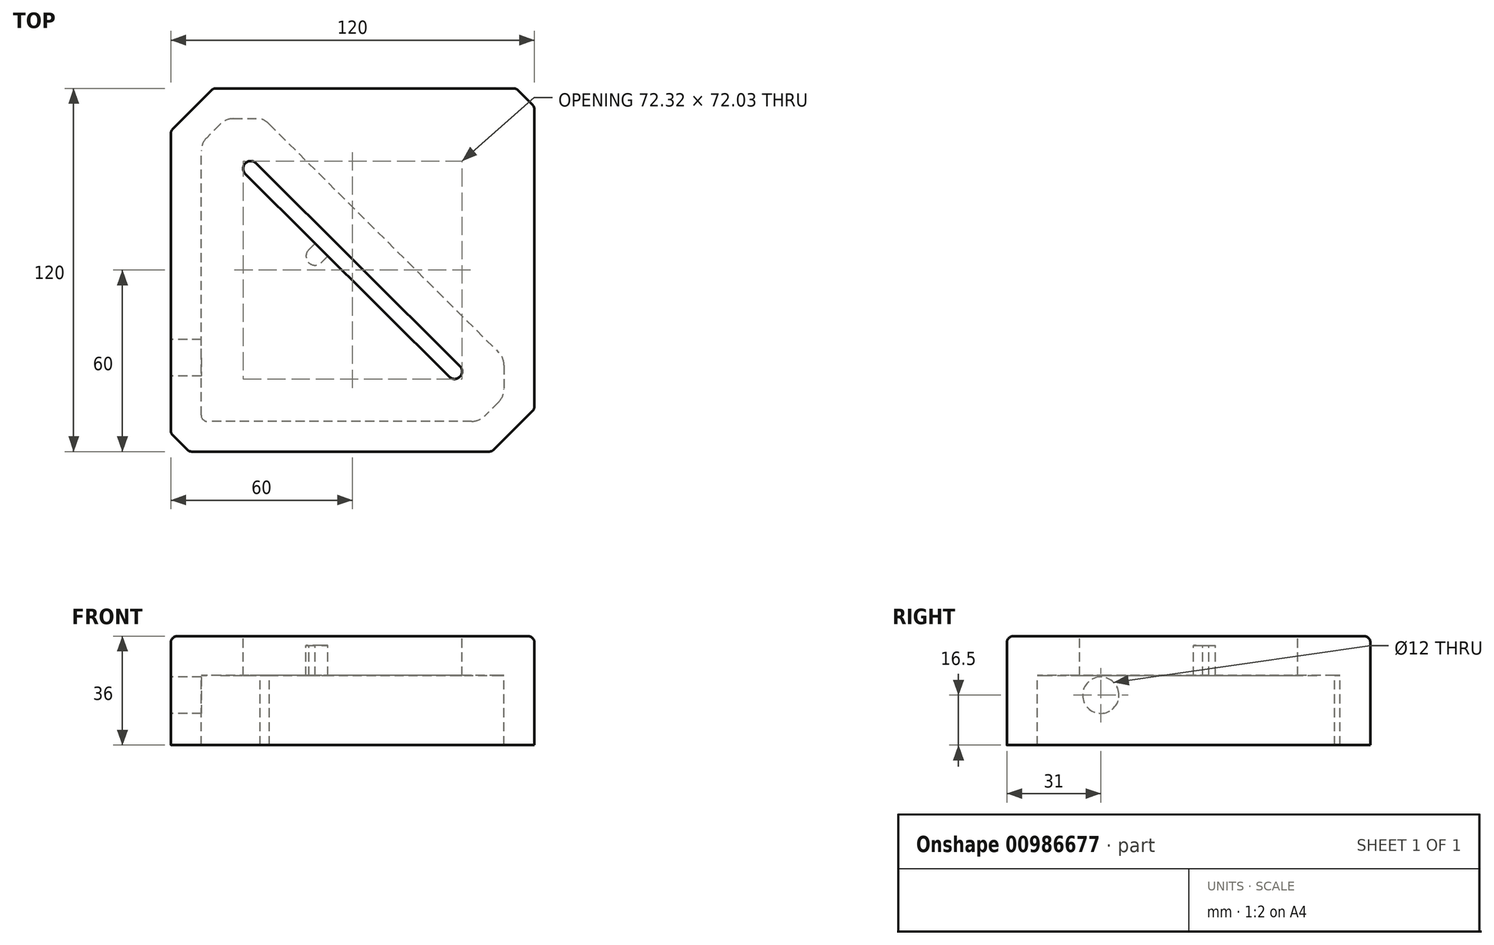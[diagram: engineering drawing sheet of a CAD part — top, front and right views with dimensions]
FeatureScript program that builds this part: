
annotation { "Feature Type Name" : "Feature", "Feature Type Description" : "" }
export const myFeature = defineFeature(function(context is Context, id is Id, definition is map)
    precondition{}
    {
        {
            var Q0;
            Q0=qCreatedBy(makeId("Top.planeOp"),FACE);
            var sketch = newSketch(context, id + "F0", { "sketchPlane" : qUnion([Q0])});
            skLineSegment(sketch, "E0.bottom", {"start": v(14, 0) * mm, "end": v(114, 0) * mm});
            skLineSegment(sketch, "E0.top", {"start": v(6, 120) * mm, "end": v(106, 120) * mm});
            skLineSegment(sketch, "E0.left", {"start": v(0, 14) * mm, "end": v(0, 114) * mm});
            skLineSegment(sketch, "E0.right", {"start": v(120, 6) * mm, "end": v(120, 106) * mm});
            skLineSegment(sketch, "E1", {"start": v(0, 114) * mm, "end": v(6, 120) * mm});
            skLineSegment(sketch, "E2", {"start": v(120, 6) * mm, "end": v(114, 0) * mm});
            skLineSegment(sketch, "E3", {"start": v(0, 14) * mm, "end": v(14, 0) * mm});
            skLineSegment(sketch, "E4", {"start": v(106, 120) * mm, "end": v(120, 106) * mm});
            skLineSegment(sketch, "E5.left", {"start": v(95.43, 91.74) * mm, "end": v(28.1, 24.72) * mm});
            skLineSegment(sketch, "E5.right", {"start": v(91.9, 95.28) * mm, "end": v(24.57, 28.26) * mm});
            skPoint(sketch, "E5.middle", {"position": v(60, 60) * mm});
            skArc(sketch, "E6", {"start": v(95.43, 91.74) * mm, "mid": v(95.43, 95.28) * mm, "end": v(91.9, 95.28) * mm});
            skArc(sketch, "E7", {"start": v(24.57, 28.26) * mm, "mid": v(24.57, 24.72) * mm, "end": v(28.1, 24.72) * mm});
            skLineSegment(sketch, "E8", {"start": v(32.45, 11.8) * mm, "end": v(108.23, 87.24) * mm});
            skLineSegment(sketch, "E9", {"start": v(110, 91.5) * mm, "end": v(110, 99.37) * mm});
            skLineSegment(sketch, "E10", {"start": v(99.37, 110) * mm, "end": v(12, 110) * mm});
            skLineSegment(sketch, "E11", {"start": v(10, 108) * mm, "end": v(10, 20.63) * mm});
            skLineSegment(sketch, "E12", {"start": v(20.63, 10) * mm, "end": v(29.51, 10) * mm});
            skArc(sketch, "E13", {"start": v(29.51, 10) * mm, "mid": v(31.1, 10.7) * mm, "end": v(32.45, 11.8) * mm});
            skPoint(sketch, "E14.orphan", {"position": v(10, 10) * mm});
            skPoint(sketch, "E15.orphan", {"position": v(30.65, 10) * mm});
            skArc(sketch, "E16", {"start": v(12, 110) * mm, "mid": v(10.59, 109.41) * mm, "end": v(10, 108) * mm});
            skArc(sketch, "E17", {"start": v(49.63, 53.2) * mm, "mid": v(49.73, 53.3) * mm, "end": v(49.84, 53.4) * mm});
            skArc(sketch, "E18.trimOffspring", {"start": v(49.8, 57.48) * mm, "mid": v(45.5, 57.56) * mm, "end": v(45.55, 53.26) * mm});
            skLineSegment(sketch, "E19", {"start": v(49.8, 57.48) * mm, "end": v(51.8, 55.36) * mm});
            skLineSegment(sketch, "E20", {"start": v(45.55, 53.26) * mm, "end": v(47.6, 51.19) * mm});
            skLineSegment(sketch, "E21", {"start": v(108.24, 103.62) * mm, "end": v(103.62, 108.24) * mm});
            skLineSegment(sketch, "E22", {"start": v(16.38, 11.76) * mm, "end": v(11.76, 16.38) * mm});
            skPoint(sketch, "E23.visualSharp", {"position": v(18.14, 10) * mm});
            skArc(sketch, "E23.filletArc", {"start": v(16.38, 11.76) * mm, "mid": v(18.33, 10.46) * mm, "end": v(20.63, 10) * mm});
            skPoint(sketch, "E24.visualSharp", {"position": v(10, 18.14) * mm});
            skArc(sketch, "E24.filletArc", {"start": v(10, 20.63) * mm, "mid": v(10.46, 18.33) * mm, "end": v(11.76, 16.38) * mm});
            skPoint(sketch, "E25.visualSharp", {"position": v(110, 101.86) * mm});
            skArc(sketch, "E25.filletArc", {"start": v(110, 99.37) * mm, "mid": v(109.54, 101.67) * mm, "end": v(108.24, 103.62) * mm});
            skPoint(sketch, "E26.visualSharp", {"position": v(101.86, 110) * mm});
            skArc(sketch, "E26.filletArc", {"start": v(103.62, 108.24) * mm, "mid": v(101.67, 109.54) * mm, "end": v(99.37, 110) * mm});
            skPoint(sketch, "E27.visualSharp", {"position": v(110, 89) * mm});
            skArc(sketch, "E27.filletArc", {"start": v(108.23, 87.24) * mm, "mid": v(109.54, 89.2) * mm, "end": v(110, 91.5) * mm});
            skSolve(sketch);
        }
        {
            var Q0;
            Q0=makeQuery(id+"F0.imprint","IMPRINT",FACE,{"disambiguationData":[TD([[makeQuery(id+"F0.imprint","IMPRINT",EDGE,{"derivedFrom":sQuery(id+"F0.wireOp",EDGE,"E5.left")}),1.0]])]});
            extrude(context, id + "F1", {"entities" : qUnion([Q0]), "depth" : 13 * mm, "offsetDistance" : 25 * mm});
        }
        {
            var Q0;
            Q0=makeQuery(id+"F0.imprint","IMPRINT",FACE,{"disambiguationData":[TD([[makeQuery(id+"F0.imprint","IMPRINT",EDGE,{"derivedFrom":sQuery(id+"F0.wireOp",EDGE,"E0.bottom")}),1.0]])]});
            extrude(context, id + "F2", {"entities" : qUnion([Q0]), "operationType" : NewBodyOperationType.ADD, "depth" : 36 * mm, "offsetDistance" : 25 * mm});
        }
        {
            var Q0;
            {var subQ4=sQuery(id+"F0.wireOp",EDGE,"E17");var subQ5=sQuery(id+"F0.wireOp",EDGE,"E5.right");var subQ8=makeQuery(id+"F0.imprint","INTERSECT",VERTEX,{"disambiguationData":[OD(1.0)],"derivedFrom":[subQ5,subQ4]});Q0=makeQuery(id+"F0.imprint","IMPRINT",FACE,{"disambiguationData":[TD([[makeQuery(id+"F0.imprint","IMPRINT",EDGE,{"disambiguationData":[TD([[subQ8,1.0]])],"derivedFrom":subQ5}),-1.0]])]});}
            extrude(context, id + "F3", {"entities" : qUnion([Q0]), "operationType" : NewBodyOperationType.ADD, "depth" : 3 * mm, "offsetDistance" : 25 * mm});
        }
        {
            var Q0;
            Q0=makeQuery(id+"F2.opExtrude","CAP_EDGE",EDGE,{"disambiguationData":[OSD([sQuery(id+"F0.wireOp",EDGE,"E0.top")])],"isStart":true});
            var Q1;
            Q1=makeQuery(id+"F2.opExtrude","SWEPT_EDGE",EDGE,{"disambiguationData":[OSD([sQuery(id+"F0.wireOp",EDGE,"E0.top"),sQuery(id+"F0.wireOp",EDGE,"E4")])]});
            var Q2;
            Q2=makeQuery(id+"F2.opExtrude","SWEPT_EDGE",EDGE,{"disambiguationData":[OSD([sQuery(id+"F0.wireOp",EDGE,"E0.right"),sQuery(id+"F0.wireOp",EDGE,"E4")])]});
            var Q3;
            Q3=makeQuery(id+"F2.opExtrude","CAP_EDGE",EDGE,{"disambiguationData":[OSD([sQuery(id+"F0.wireOp",EDGE,"E0.right")])],"isStart":true});
            var Q4;
            Q4=makeQuery(id+"F2.opExtrude","CAP_EDGE",EDGE,{"disambiguationData":[OSD([sQuery(id+"F0.wireOp",EDGE,"E4")])],"isStart":true});
            var Q5;
            Q5=makeQuery(id+"F2.opExtrude","CAP_EDGE",EDGE,{"disambiguationData":[OSD([sQuery(id+"F0.wireOp",EDGE,"E2")])],"isStart":true});
            var Q6;
            Q6=makeQuery(id+"F2.opExtrude","SWEPT_EDGE",EDGE,{"disambiguationData":[OSD([sQuery(id+"F0.wireOp",EDGE,"E0.bottom"),sQuery(id+"F0.wireOp",EDGE,"E2")])]});
            var Q7;
            Q7=makeQuery(id+"F2.opExtrude","SWEPT_EDGE",EDGE,{"disambiguationData":[OSD([sQuery(id+"F0.wireOp",EDGE,"E0.right"),sQuery(id+"F0.wireOp",EDGE,"E2")])]});
            var Q8;
            Q8=makeQuery(id+"F2.opExtrude","CAP_EDGE",EDGE,{"disambiguationData":[OSD([sQuery(id+"F0.wireOp",EDGE,"E0.bottom")])],"isStart":true});
            var Q9;
            Q9=makeQuery(id+"F2.opExtrude","SWEPT_EDGE",EDGE,{"disambiguationData":[OSD([sQuery(id+"F0.wireOp",EDGE,"E0.bottom"),sQuery(id+"F0.wireOp",EDGE,"E3")])]});
            var Q10;
            Q10=makeQuery(id+"F2.opExtrude","CAP_EDGE",EDGE,{"disambiguationData":[OSD([sQuery(id+"F0.wireOp",EDGE,"E3")])],"isStart":true});
            var Q11;
            Q11=makeQuery(id+"F2.opExtrude","SWEPT_EDGE",EDGE,{"disambiguationData":[OSD([sQuery(id+"F0.wireOp",EDGE,"E0.left"),sQuery(id+"F0.wireOp",EDGE,"E3")])]});
            var Q12;
            Q12=makeQuery(id+"F2.opExtrude","CAP_EDGE",EDGE,{"disambiguationData":[OSD([sQuery(id+"F0.wireOp",EDGE,"E0.left")])],"isStart":true});
            var Q13;
            Q13=makeQuery(id+"F2.opExtrude","CAP_EDGE",EDGE,{"disambiguationData":[OSD([sQuery(id+"F0.wireOp",EDGE,"E1")])],"isStart":true});
            var Q14;
            Q14=makeQuery(id+"F2.opExtrude","SWEPT_EDGE",EDGE,{"disambiguationData":[OSD([sQuery(id+"F0.wireOp",EDGE,"E0.left"),sQuery(id+"F0.wireOp",EDGE,"E1")])]});
            var Q15;
            Q15=makeQuery(id+"F2.opExtrude","SWEPT_EDGE",EDGE,{"disambiguationData":[OSD([sQuery(id+"F0.wireOp",EDGE,"E0.top"),sQuery(id+"F0.wireOp",EDGE,"E1")])]});
            fillet(context, id + "F4", {"entities" : qUnion([Q0, Q1, Q2, Q3, Q4, Q5, Q6, Q7, Q8, Q9, Q10, Q11, Q12, Q13, Q14, Q15]), "radius" : 2 * mm, "tangentPropagation" : true, "allowEdgeOverflow" : false});
        }
        {
            var Q0;
            Q0=makeQuery(id+"F2.opExtrude","SWEPT_FACE",FACE,{"disambiguationData":[OSD([sQuery(id+"F0.wireOp",EDGE,"E0.left")])]});
            var sketch = newSketch(context, id + "F5", { "sketchPlane" : qUnion([Q0])});
            skCircle(sketch, "E28", {"center": v(-89, 19.5) * mm, "radius": 6 * mm});
            skSolve(sketch);
        }
        {
            var Q0;
            Q0=sQuery(id+"F5.wireOp",VERTEX,"E28.center");
            var Q1;
            Q1=makeQuery(id+"F1.opExtrude","SWEPT_BODY",BODY,{"disambiguationData":[OSD([sQuery(id+"F0.wireOp",EDGE,"E5.left"),sQuery(id+"F0.wireOp",EDGE,"E5.right"),sQuery(id+"F0.wireOp",EDGE,"E6"),sQuery(id+"F0.wireOp",EDGE,"E7"),sQuery(id+"F0.wireOp",EDGE,"E8"),sQuery(id+"F0.wireOp",EDGE,"E9"),sQuery(id+"F0.wireOp",EDGE,"E10"),sQuery(id+"F0.wireOp",EDGE,"E11"),sQuery(id+"F0.wireOp",EDGE,"E12"),sQuery(id+"F0.wireOp",EDGE,"WjEH5ti4-Gntd-ozZf-Yr4r-jxueL6gdnWYW"),sQuery(id+"F0.wireOp",EDGE,"59pm3X2Q-MiUk-4We3-apMV-84U9ViCuhb4i"),sQuery(id+"F0.wireOp",EDGE,"E13"),sQuery(id+"F0.wireOp",EDGE,"AbjG9SvJ-RGuI-1kTg-4pos-58oHFgegNcMA"),sQuery(id+"F0.wireOp",EDGE,"E16")])]});
            hole(context, id + "F6", {"style" : HoleStyle.SIMPLE, "endStyle" : HoleEndStyle.BLIND, "holeDiameter" : 12 * mm, "majorDiameter" : 5 * mm, "holeDepth" : 12 * mm, "isTappedThrough" : true, "tappedDepth" : 12 * mm, "tapClearance" : 3, "locations" : qUnion([Q0]), "scope" : qUnion([Q1])});
        }
        {
            var Q0;
            Q0=makeQuery(id+"F1.opExtrude","SWEPT_BODY",BODY,{"disambiguationData":[OSD([sQuery(id+"F0.wireOp",EDGE,"E5.left"),sQuery(id+"F0.wireOp",EDGE,"E5.right"),sQuery(id+"F0.wireOp",EDGE,"E6"),sQuery(id+"F0.wireOp",EDGE,"E7"),sQuery(id+"F0.wireOp",EDGE,"E8"),sQuery(id+"F0.wireOp",EDGE,"E9"),sQuery(id+"F0.wireOp",EDGE,"E10"),sQuery(id+"F0.wireOp",EDGE,"E11"),sQuery(id+"F0.wireOp",EDGE,"E12"),sQuery(id+"F0.wireOp",EDGE,"WjEH5ti4-Gntd-ozZf-Yr4r-jxueL6gdnWYW"),sQuery(id+"F0.wireOp",EDGE,"59pm3X2Q-MiUk-4We3-apMV-84U9ViCuhb4i"),sQuery(id+"F0.wireOp",EDGE,"E13"),sQuery(id+"F0.wireOp",EDGE,"AbjG9SvJ-RGuI-1kTg-4pos-58oHFgegNcMA"),sQuery(id+"F0.wireOp",EDGE,"E16")])]});
            var Q1;
            {var subQ0=sQuery(id+"F0.wireOp",EDGE,"E16");var subQ1=sQuery(id+"F0.wireOp",EDGE,"AbjG9SvJ-RGuI-1kTg-4pos-58oHFgegNcMA");var subQ2=sQuery(id+"F0.wireOp",EDGE,"E13");var subQ3=sQuery(id+"F0.wireOp",EDGE,"59pm3X2Q-MiUk-4We3-apMV-84U9ViCuhb4i");var subQ4=sQuery(id+"F0.wireOp",EDGE,"WjEH5ti4-Gntd-ozZf-Yr4r-jxueL6gdnWYW");var subQ5=sQuery(id+"F0.wireOp",EDGE,"E12");var subQ6=sQuery(id+"F0.wireOp",EDGE,"E11");var subQ7=sQuery(id+"F0.wireOp",EDGE,"E10");var subQ8=sQuery(id+"F0.wireOp",EDGE,"E9");var subQ9=sQuery(id+"F0.wireOp",EDGE,"E8");var subQ10=sQuery(id+"F0.wireOp",EDGE,"E0.bottom");Q1=makeQuery(id+"F4.opFillet","BLEND_EDGE",EDGE,{"blendedFrom":[makeQuery(id+"F2.opExtrude","CAP_EDGE",EDGE,{"disambiguationData":[OSD([subQ10])],"isStart":true}),makeQuery(id+"F2.boolean.opBoolean","MERGE",FACE,{"derivedFrom":[makeQuery(id+"F1.opExtrude","CAP_FACE",FACE,{"disambiguationData":[OSD([sQuery(id+"F0.wireOp",EDGE,"E5.left"),sQuery(id+"F0.wireOp",EDGE,"E5.right"),sQuery(id+"F0.wireOp",EDGE,"E6"),sQuery(id+"F0.wireOp",EDGE,"E7"),subQ9,subQ8,subQ7,subQ6,subQ5,subQ4,subQ3,subQ2,subQ1,subQ0])],"isStart":true}),makeQuery(id+"F2.opExtrude","CAP_FACE",FACE,{"disambiguationData":[OSD([subQ10,sQuery(id+"F0.wireOp",EDGE,"E0.top"),sQuery(id+"F0.wireOp",EDGE,"E0.left"),sQuery(id+"F0.wireOp",EDGE,"E0.right"),sQuery(id+"F0.wireOp",EDGE,"E1"),sQuery(id+"F0.wireOp",EDGE,"E2"),sQuery(id+"F0.wireOp",EDGE,"E3"),sQuery(id+"F0.wireOp",EDGE,"E4"),subQ9,subQ8,subQ7,subQ6,subQ5,subQ4,subQ3,subQ2,subQ1,subQ0])],"isStart":true})]})],"blendedInto":[makeQuery(id+"F2.boolean.opBoolean","MERGE",FACE,{"derivedFrom":[makeQuery(id+"F1.opExtrude","CAP_FACE",FACE,{"disambiguationData":[OSD([sQuery(id+"F0.wireOp",EDGE,"E5.left"),sQuery(id+"F0.wireOp",EDGE,"E5.right"),sQuery(id+"F0.wireOp",EDGE,"E6"),sQuery(id+"F0.wireOp",EDGE,"E7"),subQ9,subQ8,subQ7,subQ6,subQ5,subQ4,subQ3,subQ2,subQ1,subQ0])],"isStart":true}),makeQuery(id+"F2.opExtrude","CAP_FACE",FACE,{"disambiguationData":[OSD([subQ10,sQuery(id+"F0.wireOp",EDGE,"E0.top"),sQuery(id+"F0.wireOp",EDGE,"E0.left"),sQuery(id+"F0.wireOp",EDGE,"E0.right"),sQuery(id+"F0.wireOp",EDGE,"E1"),sQuery(id+"F0.wireOp",EDGE,"E2"),sQuery(id+"F0.wireOp",EDGE,"E3"),sQuery(id+"F0.wireOp",EDGE,"E4"),subQ9,subQ8,subQ7,subQ6,subQ5,subQ4,subQ3,subQ2,subQ1,subQ0])],"isStart":true})]})]});}
            transform(context, id + "F7", {"entities" : qUnion([Q0]), "transformType" : TransformType.ROTATION, "transformAxis" : qUnion([Q1]), "angle" : 180 * degree, "makeCopy" : false});
        }
    });
